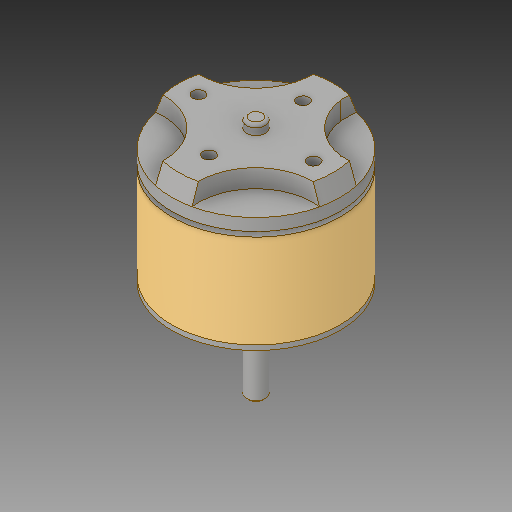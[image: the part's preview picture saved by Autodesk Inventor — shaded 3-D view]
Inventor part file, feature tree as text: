
AUTODESK INVENTOR PART (.ipt)
format: ipt  version: 2019 (Build 230136000, 136)  size: 202,240 bytes
history: imported  units: mm
features: imported_body x1
ambient origin geometry x8: Origin, YZ Plane, XZ Plane, XY Plane, X Axis, Y Axis, Z Axis, Center Point
bodies: Solide1 (imported_parasolid), Body2 (imported_parasolid)
feature tree (1):
  imported_body  NMx_Import_Brep_tag  [imported B-rep: ~20 faces, bbox_mm=[26.276184, 5.0, 20.16249]]
